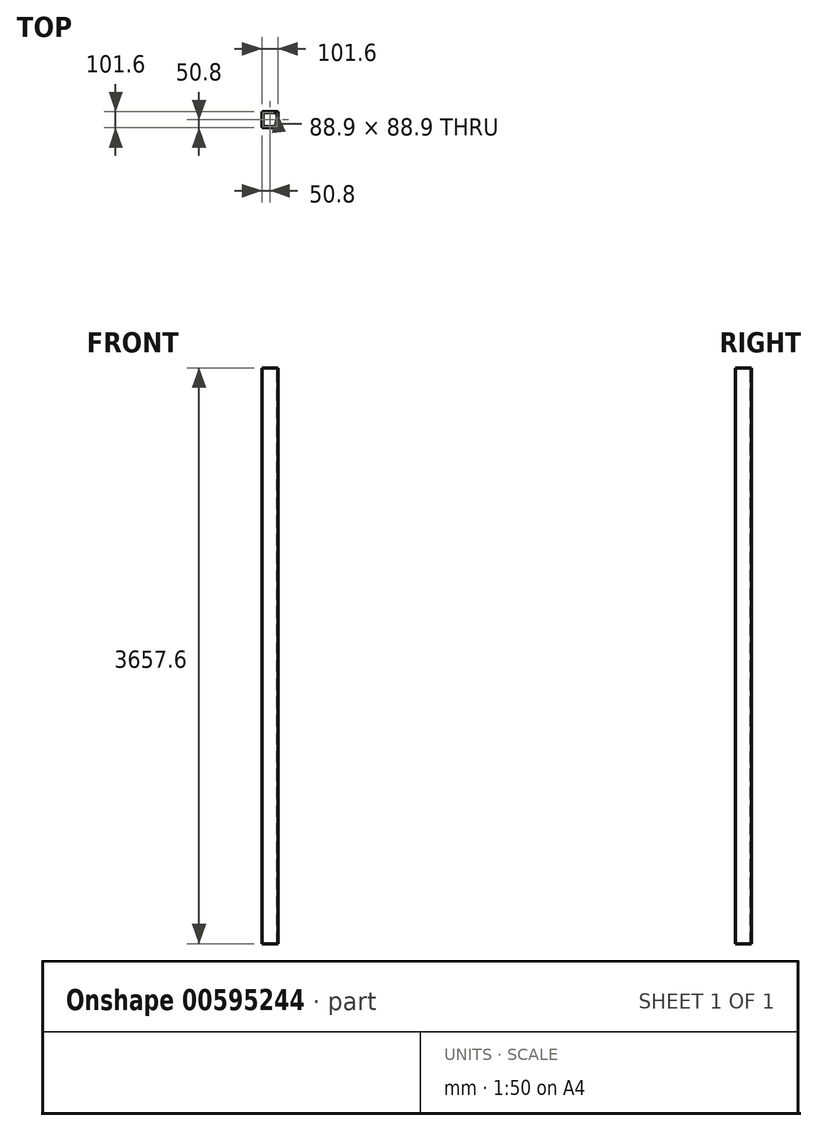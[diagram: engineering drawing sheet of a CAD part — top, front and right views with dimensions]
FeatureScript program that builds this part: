
annotation { "Feature Type Name" : "Feature", "Feature Type Description" : "" }
export const myFeature = defineFeature(function(context is Context, id is Id, definition is map)
    precondition{}
    {
        {
            var Q0;
            Q0=qCreatedBy(makeId("Top.planeOp"),FACE);
            var sketch = newSketch(context, id + "F0", { "sketchPlane" : qUnion([Q0])});
            skLineSegment(sketch, "E0.bottom", {"start": v(0, 0) * mm, "end": v(101.6, 0) * mm});
            skLineSegment(sketch, "E0.top", {"start": v(0, -101.6) * mm, "end": v(101.6, -101.6) * mm});
            skLineSegment(sketch, "E0.left", {"start": v(0, 0) * mm, "end": v(0, -101.6) * mm});
            skLineSegment(sketch, "E0.right", {"start": v(101.6, 0) * mm, "end": v(101.6, -101.6) * mm});
            skSolve(sketch);
        }
        {
            var Q0;
            Q0 = qSketchRegion(id + "F0", true);
            extrude(context, id + "F1", {"entities" : qUnion([Q0]), "depth" : 3657.6 * mm, "offsetDistance" : 25.4 * mm});
        }
        {
            var Q0;
            Q0=makeQuery(id+"F1.opExtrude","CAP_FACE",FACE,{"disambiguationData":[OSD([sQuery(id+"F0.wireOp",EDGE,"E0.bottom"),sQuery(id+"F0.wireOp",EDGE,"E0.top"),sQuery(id+"F0.wireOp",EDGE,"E0.left"),sQuery(id+"F0.wireOp",EDGE,"E0.right")])],"isStart":false});
            var sketch = newSketch(context, id + "F2", { "sketchPlane" : qUnion([Q0])});
            skLineSegment(sketch, "E1.bottom", {"start": v(95.25, -95.25) * mm, "end": v(6.35, -95.25) * mm});
            skLineSegment(sketch, "E1.top", {"start": v(95.25, -6.35) * mm, "end": v(6.35, -6.35) * mm});
            skLineSegment(sketch, "E1.left", {"start": v(95.25, -95.25) * mm, "end": v(95.25, -6.35) * mm});
            skLineSegment(sketch, "E1.right", {"start": v(6.35, -95.25) * mm, "end": v(6.35, -6.35) * mm});
            skPoint(sketch, "E1.middle", {"position": v(50.8, -50.8) * mm});
            skPoint(sketch, "E1.middle.positionSnap0", {"position": v(50.8, 0) * mm});
            skPoint(sketch, "E1.middle.positionSnap1", {"position": v(101.6, -50.8) * mm});
            skPoint(sketch, "E1.centerSnap0", {"position": v(50.8, 0) * mm});
            skPoint(sketch, "E1.centerSnap1", {"position": v(101.6, -50.8) * mm});
            skSolve(sketch);
        }
        {
            var Q0;
            Q0=makeQuery(id+"F2.imprint","IMPRINT",FACE,{"disambiguationData":[TD([[makeQuery(id+"F2.imprint","IMPRINT",EDGE,{"derivedFrom":sQuery(id+"F2.wireOp",EDGE,"E1.bottom")}),-1.0]])]});
            extrude(context, id + "F3", {"entities" : qUnion([Q0]), "operationType" : NewBodyOperationType.REMOVE, "oppositeDirection" : true, "depth" : 3657.6 * mm, "offsetDistance" : 25.4 * mm});
        }
        {
            var Q0;
            Q0=makeQuery(id+"F1.opExtrude","CAP_FACE",FACE,{"disambiguationData":[OSD([sQuery(id+"F0.wireOp",EDGE,"E0.bottom"),sQuery(id+"F0.wireOp",EDGE,"E0.top"),sQuery(id+"F0.wireOp",EDGE,"E0.left"),sQuery(id+"F0.wireOp",EDGE,"E0.right")])],"isStart":false});
            var sketch = newSketch(context, id + "F4", { "sketchPlane" : qUnion([Q0])});
            skLineSegment(sketch, "E2.bottom", {"start": v(95.25, -95.25) * mm, "end": v(6.35, -95.25) * mm});
            skLineSegment(sketch, "E2.top", {"start": v(95.25, -6.35) * mm, "end": v(6.35, -6.35) * mm});
            skLineSegment(sketch, "E2.left", {"start": v(95.25, -95.25) * mm, "end": v(95.25, -6.35) * mm});
            skLineSegment(sketch, "E2.right", {"start": v(6.35, -95.25) * mm, "end": v(6.35, -6.35) * mm});
            skPoint(sketch, "E2.middle", {"position": v(50.8, -50.8) * mm});
            skPoint(sketch, "E2.middle.positionSnap0", {"position": v(95.25, -50.8) * mm});
            skPoint(sketch, "E2.middle.positionSnap1", {"position": v(50.8, -95.25) * mm});
            skPoint(sketch, "E2.centerSnap0", {"position": v(95.25, -50.8) * mm});
            skPoint(sketch, "E2.centerSnap1", {"position": v(50.8, -95.25) * mm});
            skSolve(sketch);
        }
        {
            var Q0;
            Q0=makeQuery(id+"F4.imprint","IMPRINT",FACE,{"disambiguationData":[TD([[makeQuery(id+"F4.imprint","IMPRINT",EDGE,{"derivedFrom":sQuery(id+"F4.wireOp",EDGE,"E2.bottom")}),-1.0]])]});
            extrude(context, id + "F5", {"entities" : qUnion([Q0]), "depth" : 254 * mm, "offsetDistance" : 25.4 * mm});
        }
        {
            var Q0;
            Q0=makeQuery(id+"F5.opExtrude","SWEPT_FACE",FACE,{"disambiguationData":[OSD([sQuery(id+"F4.wireOp",EDGE,"E2.left")])]});
            var sketch = newSketch(context, id + "F6", { "sketchPlane" : qUnion([Q0])});
            skLineSegment(sketch, "E3.bottom", {"start": v(-95.25, 3911.6) * mm, "end": v(-6.35, 3911.6) * mm});
            skLineSegment(sketch, "E3.top", {"start": v(-95.25, 3822.7) * mm, "end": v(-6.35, 3822.7) * mm});
            skLineSegment(sketch, "E3.left", {"start": v(-95.25, 3911.6) * mm, "end": v(-95.25, 3822.7) * mm});
            skLineSegment(sketch, "E3.right", {"start": v(-6.35, 3911.6) * mm, "end": v(-6.35, 3822.7) * mm});
            skSolve(sketch);
        }
        {
            var Q0;
            Q0=makeQuery(id+"F6.imprint","IMPRINT",FACE,{"disambiguationData":[TD([[makeQuery(id+"F6.imprint","IMPRINT",EDGE,{"derivedFrom":sQuery(id+"F6.wireOp",EDGE,"E3.bottom")}),-1.0]])]});
            extrude(context, id + "F7", {"entities" : qUnion([Q0]), "operationType" : NewBodyOperationType.ADD, "depth" : 254 * mm, "offsetDistance" : 25.4 * mm});
        }
        {
            var Q0;
            Q0=makeQuery(id+"F5.opExtrude","SWEPT_BODY",BODY,{"disambiguationData":[OSD([sQuery(id+"F4.wireOp",EDGE,"E2.bottom"),sQuery(id+"F4.wireOp",EDGE,"E2.top"),sQuery(id+"F4.wireOp",EDGE,"E2.left"),sQuery(id+"F4.wireOp",EDGE,"E2.right")])]});
            transform(context, id + "F8", {"entities" : qUnion([Q0]), "transformType" : TransformType.TRANSLATION_3D, "dx" : 0 * mm, "dy" : 0 * mm, "dz" : -152.4 * mm, "makeCopy" : false});
        }
        {
            var Q0;
            Q0=makeQuery(id+"F7.opExtrude","CAP_FACE",FACE,{"disambiguationData":[OSD([sQuery(id+"F6.wireOp",EDGE,"E3.bottom"),sQuery(id+"F6.wireOp",EDGE,"E3.top"),sQuery(id+"F6.wireOp",EDGE,"E3.left"),sQuery(id+"F6.wireOp",EDGE,"E3.right")])],"isStart":false});
            var sketch = newSketch(context, id + "F9", { "sketchPlane" : qUnion([Q0])});
            skLineSegment(sketch, "E4.bottom", {"start": v(0, 3658.34) * mm, "end": v(-101.6, 3658.34) * mm});
            skLineSegment(sketch, "E4.top", {"start": v(0, 3771.16) * mm, "end": v(-101.6, 3771.16) * mm});
            skLineSegment(sketch, "E4.left", {"start": v(0, 3658.34) * mm, "end": v(0, 3771.16) * mm});
            skLineSegment(sketch, "E4.right", {"start": v(-101.6, 3658.34) * mm, "end": v(-101.6, 3771.16) * mm});
            skPoint(sketch, "E4.middle", {"position": v(-50.8, 3714.75) * mm});
            skPoint(sketch, "E4.middle.positionSnap0", {"position": v(-95.25, 3714.75) * mm});
            skPoint(sketch, "E4.middle.positionSnap1", {"position": v(-50.8, 3759.2) * mm});
            skPoint(sketch, "E4.centerSnap0", {"position": v(-95.25, 3714.75) * mm});
            skPoint(sketch, "E4.centerSnap1", {"position": v(-50.8, 3759.2) * mm});
            skSolve(sketch);
        }
        {
            var Q0;
            Q0 = qSketchRegion(id + "F9", true);
            extrude(context, id + "F10", {"entities" : qUnion([Q0]), "operationType" : NewBodyOperationType.ADD, "depth" : 3251.2 * mm, "offsetDistance" : 25.4 * mm});
        }
        {
            var Q0;
            Q0=makeQuery(id+"F5.opExtrude","SWEPT_BODY",BODY,{"disambiguationData":[OSD([sQuery(id+"F4.wireOp",EDGE,"E2.bottom"),sQuery(id+"F4.wireOp",EDGE,"E2.top"),sQuery(id+"F4.wireOp",EDGE,"E2.left"),sQuery(id+"F4.wireOp",EDGE,"E2.right")])]});
            deleteBodies(context, id + "F11", {"entities" : qUnion([Q0])});
        }
    });
